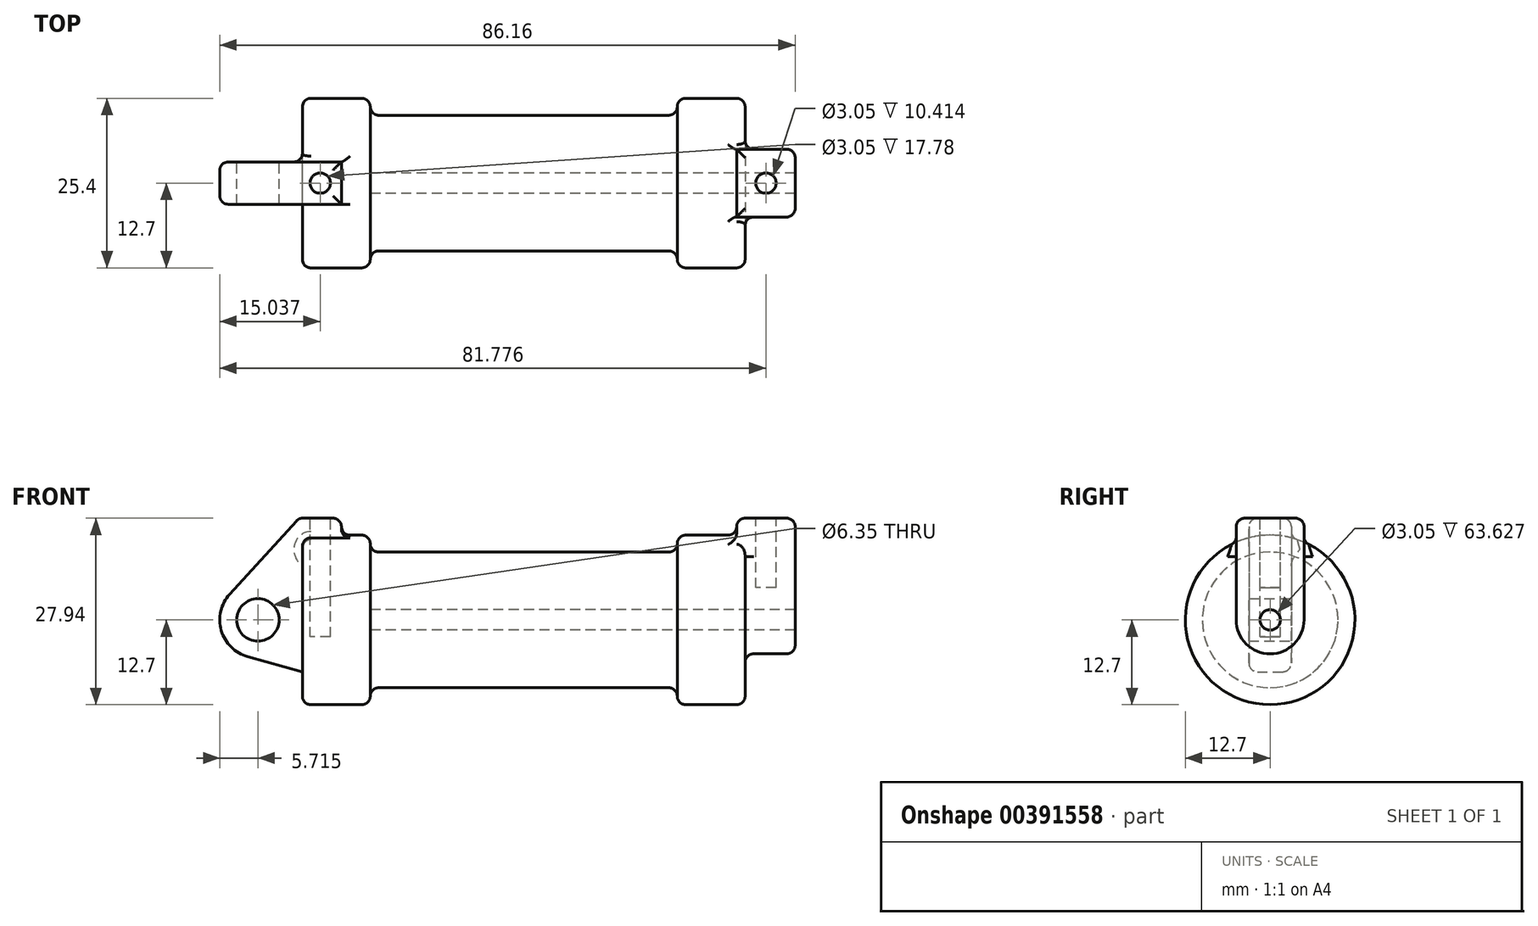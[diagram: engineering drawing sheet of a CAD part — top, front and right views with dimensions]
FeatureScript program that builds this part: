
annotation { "Feature Type Name" : "Feature", "Feature Type Description" : "" }
export const myFeature = defineFeature(function(context is Context, id is Id, definition is map)
    precondition{}
    {
        {
            var Q0;
            Q0=qCreatedBy(makeId("Front.planeOp"),FACE);
            var sketch = newSketch(context, id + "F0", { "sketchPlane" : qUnion([Q0])});
            skLineSegment(sketch, "E0", {"start": v(0, 0) * mm, "end": v(0, 12.7) * mm});
            skLineSegment(sketch, "E1", {"start": v(0, 12.7) * mm, "end": v(10.16, 12.7) * mm});
            skLineSegment(sketch, "E2", {"start": v(10.16, 12.7) * mm, "end": v(10.16, 10.16) * mm});
            skLineSegment(sketch, "E3", {"start": v(10.16, 10.16) * mm, "end": v(56.13, 10.16) * mm});
            skLineSegment(sketch, "E4", {"start": v(56.13, 10.16) * mm, "end": v(56.13, 12.7) * mm});
            skLineSegment(sketch, "E5", {"start": v(56.13, 12.7) * mm, "end": v(66.3, 12.7) * mm});
            skLineSegment(sketch, "E6", {"start": v(66.3, 12.7) * mm, "end": v(66.3, 0) * mm});
            skLineSegment(sketch, "E7", {"start": v(66.3, 0) * mm, "end": v(0, 0) * mm});
            skLineSegment(sketch, "E8", {"start": v(5.84, 15.24) * mm, "end": v(-0.5, 15.24) * mm});
            skLineSegment(sketch, "E9", {"start": v(-0.5, 15.24) * mm, "end": v(-10.88, 3.85) * mm});
            skLineSegment(sketch, "E10", {"start": v(0, 0) * mm, "end": v(-6.65, 0) * mm});
            skCircle(sketch, "E11", {"center": v(-6.65, 0) * mm, "radius": 5.72 * mm});
            skCircle(sketch, "E12", {"center": v(-6.65, 0) * mm, "radius": 3.18 * mm});
            skLineSegment(sketch, "E13", {"start": v(5.84, 15.24) * mm, "end": v(5.84, -9.4) * mm});
            skLineSegment(sketch, "E14", {"start": v(5.84, -9.4) * mm, "end": v(-8.18, -5.5) * mm});
            skSolve(sketch);
        }
        {
            var Q0;
            {var subQ0=sQuery(id+"F0.wireOp",EDGE,"E2");Q0=makeQuery(id+"F0.imprint","IMPRINT",FACE,{"disambiguationData":[TD([[makeQuery(id+"F0.imprint","IMPRINT",EDGE,{"derivedFrom":subQ0}),-1.0]])]});}
            var Q1;
            {var subQ0=sQuery(id+"F0.wireOp",EDGE,"E2");Q1=makeQuery(id+"F0.imprint","IMPRINT",FACE,{"disambiguationData":[TD([[makeQuery(id+"F0.imprint","IMPRINT",EDGE,{"derivedFrom":subQ0}),-1.0]])]});}
            var Q2;
            {var subQ0=sQuery(id+"F0.wireOp",EDGE,"E0");Q2=makeQuery(id+"F0.imprint","IMPRINT",FACE,{"disambiguationData":[TD([[makeQuery(id+"F0.imprint","IMPRINT",EDGE,{"derivedFrom":subQ0}),-1.0]])]});}
            var Q3;
            Q3=sQuery(id+"F0.wireOp",EDGE,"E7");
            revolve(context, id + "F1", {"entities" : qUnion([Q0, Q1, Q2]), "axis" : qUnion([Q3]), "revolveType" : RevolveType.FULL});
        }
        {
            var Q0;
            {var subQ1=sQuery(id+"F0.wireOp",EDGE,"E0");Q0=makeQuery(id+"F0.imprint","IMPRINT",FACE,{"disambiguationData":[TD([[makeQuery(id+"F0.imprint","IMPRINT",EDGE,{"derivedFrom":subQ1}),1.0]])]});}
            var Q1;
            {var subQ0=sQuery(id+"F0.wireOp",EDGE,"E14");Q1=makeQuery(id+"F0.imprint","IMPRINT",FACE,{"disambiguationData":[TD([[makeQuery(id+"F0.imprint","IMPRINT",EDGE,{"derivedFrom":subQ0}),-1.0]])]});}
            var Q2;
            {var subQ5=sQuery(id+"F0.wireOp",EDGE,"E12");Q2=makeQuery(id+"F0.imprint","IMPRINT",FACE,{"disambiguationData":[TD([[makeQuery(id+"F0.imprint","IMPRINT",EDGE,{"derivedFrom":subQ5}),-1.0]])]});}
            var Q3;
            {var subQ0=sQuery(id+"F0.wireOp",EDGE,"E0");Q3=makeQuery(id+"F0.imprint","IMPRINT",FACE,{"disambiguationData":[TD([[makeQuery(id+"F0.imprint","IMPRINT",EDGE,{"derivedFrom":subQ0}),-1.0]])]});}
            extrude(context, id + "F2", {"entities" : qUnion([Q0, Q1, Q2, Q3]), "operationType" : NewBodyOperationType.ADD, "endBound" : BoundingType.SYMMETRIC, "depth" : 6.35 * mm});
        }
        {
            var Q0;
            Q0=makeQuery(id+"F1.opRevolve","SWEPT_FACE",FACE,{"disambiguationData":[OSD([sQuery(id+"F0.wireOp",EDGE,"E6")])]});
            var sketch = newSketch(context, id + "F3", { "sketchPlane" : qUnion([Q0])});
            skArc(sketch, "E15", {"start": v(-5.08, 0) * mm, "mid": v(0, -5.08) * mm, "end": v(5.08, 0) * mm});
            skCircle(sketch, "E16", {"center": v(0, 0) * mm, "radius": 1.52 * mm});
            skLineSegment(sketch, "E17", {"start": v(5.08, 0) * mm, "end": v(5.08, 15.24) * mm});
            skLineSegment(sketch, "E18", {"start": v(-5.08, 0) * mm, "end": v(-5.08, 15.24) * mm});
            skLineSegment(sketch, "E19", {"start": v(-5.08, 15.24) * mm, "end": v(5.08, 15.24) * mm});
            skSolve(sketch);
        }
        {
            var Q0;
            Q0 = qSketchRegion(id + "F3", true);
            extrude(context, id + "F4", {"entities" : qUnion([Q0]), "operationType" : NewBodyOperationType.ADD, "depth" : 7.5 * mm, "hasSecondDirection" : true, "secondDirectionOppositeDirection" : true, "secondDirectionDepth" : 1.27 * mm});
        }
        {
            var Q0;
            Q0=makeQuery(id+"F3.imprint","IMPRINT",FACE,{"disambiguationData":[TD([[makeQuery(id+"F3.imprint","IMPRINT",EDGE,{"derivedFrom":sQuery(id+"F3.wireOp",EDGE,"E16")}),1.0]])]});
            var Q1;
            Q1=makeQuery(id+"F1.opRevolve","SWEPT_FACE",FACE,{"disambiguationData":[OSD([sQuery(id+"F0.wireOp",EDGE,"E2")])]});
            extrude(context, id + "F5", {"entities" : qUnion([Q0]), "operationType" : NewBodyOperationType.REMOVE, "endBound" : BoundingType.UP_TO_SURFACE, "oppositeDirection" : true, "endBoundEntityFace" : qUnion([Q1]), "depth" : 25.4 * mm});
        }
        {
            var Q0;
            Q0=makeQuery(id+"F4.opExtrude","SWEPT_FACE",FACE,{"disambiguationData":[OSD([sQuery(id+"F3.wireOp",EDGE,"E19")])]});
            var sketch = newSketch(context, id + "F6", { "sketchPlane" : qUnion([Q0])});
            skLineSegment(sketch, "E20.bottom", {"start": v(65.02, 5.08) * mm, "end": v(73.79, 5.08) * mm});
            skLineSegment(sketch, "E20.top", {"start": v(65.02, -5.08) * mm, "end": v(73.79, -5.08) * mm});
            skLineSegment(sketch, "E20.left", {"start": v(65.02, 5.08) * mm, "end": v(65.02, -5.08) * mm});
            skLineSegment(sketch, "E20.right", {"start": v(73.79, 5.08) * mm, "end": v(73.79, -5.08) * mm});
            skCircle(sketch, "E21", {"center": v(69.4, 0) * mm, "radius": 1.52 * mm});
            skPoint(sketch, "E21.centerSnap0", {"position": v(73.79, 0) * mm});
            skPoint(sketch, "E21.centerSnap1", {"position": v(69.4, 5.08) * mm});
            skSolve(sketch);
        }
        {
            var Q0;
            Q0=makeQuery(id+"F6.imprint","IMPRINT",FACE,{"disambiguationData":[TD([[makeQuery(id+"F6.imprint","IMPRINT",EDGE,{"derivedFrom":sQuery(id+"F6.wireOp",EDGE,"E21")}),1.0]])]});
            extrude(context, id + "F7", {"entities" : qUnion([Q0]), "operationType" : NewBodyOperationType.REMOVE, "oppositeDirection" : true, "depth" : 10.4 * mm});
        }
        {
            var Q0;
            Q0=makeQuery(id+"F2.opExtrude","SWEPT_FACE",FACE,{"disambiguationData":[OSD([sQuery(id+"F0.wireOp",EDGE,"E8")])]});
            var sketch = newSketch(context, id + "F8", { "sketchPlane" : qUnion([Q0])});
            skLineSegment(sketch, "E22.bottom", {"start": v(-0.5, 3.18) * mm, "end": v(5.84, 3.18) * mm});
            skLineSegment(sketch, "E22.top", {"start": v(-0.5, -3.18) * mm, "end": v(5.84, -3.18) * mm});
            skLineSegment(sketch, "E22.left", {"start": v(-0.5, 3.18) * mm, "end": v(-0.5, -3.18) * mm});
            skLineSegment(sketch, "E22.right", {"start": v(5.84, 3.18) * mm, "end": v(5.84, -3.18) * mm});
            skCircle(sketch, "E23", {"center": v(2.67, 0) * mm, "radius": 1.52 * mm});
            skPoint(sketch, "E23.centerSnap0", {"position": v(2.67, 3.18) * mm});
            skPoint(sketch, "E23.centerSnap1", {"position": v(5.84, 0) * mm});
            skSolve(sketch);
        }
        {
            var Q0;
            Q0=makeQuery(id+"F8.imprint","IMPRINT",FACE,{"disambiguationData":[TD([[makeQuery(id+"F8.imprint","IMPRINT",EDGE,{"derivedFrom":sQuery(id+"F8.wireOp",EDGE,"E23")}),1.0]])]});
            extrude(context, id + "F9", {"entities" : qUnion([Q0]), "operationType" : NewBodyOperationType.REMOVE, "oppositeDirection" : true, "depth" : 17.78 * mm});
        }
        {
            var Q0;
            Q0=makeQuery(id+"F1.opRevolve","SWEPT_EDGE",EDGE,{"disambiguationData":[OSD([sQuery(id+"F0.wireOp",EDGE,"E1"),sQuery(id+"F0.wireOp",EDGE,"E2")])]});
            var Q1;
            Q1=makeQuery(id+"F1.opRevolve","SWEPT_EDGE",EDGE,{"disambiguationData":[OSD([sQuery(id+"F0.wireOp",EDGE,"E4"),sQuery(id+"F0.wireOp",EDGE,"E5")])]});
            var Q2;
            Q2=makeQuery(id+"F1.opRevolve","SWEPT_EDGE",EDGE,{"disambiguationData":[OSD([sQuery(id+"F0.wireOp",EDGE,"E5"),sQuery(id+"F0.wireOp",EDGE,"E6")])]});
            var Q3;
            Q3=makeQuery(id+"F1.opRevolve","SWEPT_EDGE",EDGE,{"disambiguationData":[OSD([sQuery(id+"F0.wireOp",EDGE,"E0"),sQuery(id+"F0.wireOp",EDGE,"E1")])]});
            var Q4;
            Q4=makeQuery(id+"F2.opExtrude","CAP_EDGE",EDGE,{"disambiguationData":[OSD([sQuery(id+"F0.wireOp",EDGE,"E14")])],"isStart":true});
            var Q5;
            Q5=makeQuery(id+"F2.opExtrude","CAP_EDGE",EDGE,{"disambiguationData":[OSD([sQuery(id+"F0.wireOp",EDGE,"E11")])],"isStart":true});
            var Q6;
            Q6=makeQuery(id+"F2.opExtrude","CAP_EDGE",EDGE,{"disambiguationData":[OSD([sQuery(id+"F0.wireOp",EDGE,"E14")])],"isStart":false});
            var Q7;
            Q7=makeQuery(id+"F2.opExtrude","CAP_EDGE",EDGE,{"disambiguationData":[OSD([sQuery(id+"F0.wireOp",EDGE,"E11")])],"isStart":false});
            var Q8;
            Q8=makeQuery(id+"F2.opExtrude","CAP_EDGE",EDGE,{"disambiguationData":[OSD([sQuery(id+"F0.wireOp",EDGE,"E8")])],"isStart":false});
            var Q9;
            Q9=makeQuery(id+"F2.opExtrude","SWEPT_EDGE",EDGE,{"disambiguationData":[OSD([sQuery(id+"F0.wireOp",EDGE,"E8"),sQuery(id+"F0.wireOp",EDGE,"E13")])]});
            var Q10;
            Q10=makeQuery(id+"F2.opExtrude","CAP_EDGE",EDGE,{"disambiguationData":[OSD([sQuery(id+"F0.wireOp",EDGE,"E8")])],"isStart":true});
            var Q11;
            Q11=makeQuery(id+"F2.opExtrude","SWEPT_EDGE",EDGE,{"disambiguationData":[OSD([sQuery(id+"F0.wireOp",EDGE,"E8"),sQuery(id+"F0.wireOp",EDGE,"E9")])]});
            var Q12;
            Q12=makeQuery(id+"F4.opExtrude","CAP_EDGE",EDGE,{"disambiguationData":[OSD([sQuery(id+"F3.wireOp",EDGE,"E19")])],"isStart":true});
            var Q13;
            Q13=makeQuery(id+"F4.opExtrude","SWEPT_EDGE",EDGE,{"disambiguationData":[OSD([sQuery(id+"F3.wireOp",EDGE,"E18"),sQuery(id+"F3.wireOp",EDGE,"E19")])]});
            var Q14;
            Q14=makeQuery(id+"F4.opExtrude","CAP_EDGE",EDGE,{"disambiguationData":[OSD([sQuery(id+"F3.wireOp",EDGE,"E19")])],"isStart":false});
            var Q15;
            Q15=makeQuery(id+"F4.opExtrude","SWEPT_EDGE",EDGE,{"disambiguationData":[OSD([sQuery(id+"F3.wireOp",EDGE,"E17"),sQuery(id+"F3.wireOp",EDGE,"E19")])]});
            var Q16;
            Q16=makeQuery(id+"F4.opExtrude","CAP_EDGE",EDGE,{"disambiguationData":[OSD([sQuery(id+"F3.wireOp",EDGE,"E18")])],"isStart":false});
            var Q17;
            Q17=makeQuery(id+"F4.boolean.opBoolean","INTERSECT",EDGE,{"derivedFrom":[makeQuery(id+"F1.opRevolve","SWEPT_FACE",FACE,{"disambiguationData":[OSD([sQuery(id+"F0.wireOp",EDGE,"E5")])]}),makeQuery(id+"F4.opExtrude","CAP_FACE",FACE,{"disambiguationData":[OSD([sQuery(id+"F3.wireOp",EDGE,"E15"),sQuery(id+"F3.wireOp",EDGE,"E16"),sQuery(id+"F3.wireOp",EDGE,"E17"),sQuery(id+"F3.wireOp",EDGE,"E18"),sQuery(id+"F3.wireOp",EDGE,"E19")])],"isStart":true})]});
            var Q18;
            Q18=makeQuery(id+"F1.opRevolve","SWEPT_EDGE",EDGE,{"disambiguationData":[OSD([sQuery(id+"F0.wireOp",EDGE,"E3"),sQuery(id+"F0.wireOp",EDGE,"E4")])]});
            var Q19;
            Q19=makeQuery(id+"F2.boolean.opBoolean","INTERSECT",EDGE,{"derivedFrom":[makeQuery(id+"F1.opRevolve","SWEPT_FACE",FACE,{"disambiguationData":[OSD([sQuery(id+"F0.wireOp",EDGE,"E1")])]}),makeQuery(id+"F2.opExtrude","SWEPT_FACE",FACE,{"disambiguationData":[OSD([sQuery(id+"F0.wireOp",EDGE,"E13")])]})]});
            var Q20;
            Q20=makeQuery(id+"F1.opRevolve","SWEPT_EDGE",EDGE,{"disambiguationData":[OSD([sQuery(id+"F0.wireOp",EDGE,"E2"),sQuery(id+"F0.wireOp",EDGE,"E3")])]});
            var Q21;
            Q21=makeQuery(id+"F2.boolean.opBoolean","INTERSECT",EDGE,{"derivedFrom":[makeQuery(id+"F1.opRevolve","SWEPT_FACE",FACE,{"disambiguationData":[OSD([sQuery(id+"F0.wireOp",EDGE,"E1")])]}),makeQuery(id+"F2.opExtrude","CAP_FACE",FACE,{"disambiguationData":[OSD([sQuery(id+"F0.wireOp",EDGE,"E8"),sQuery(id+"F0.wireOp",EDGE,"E9"),sQuery(id+"F0.wireOp",EDGE,"E11"),sQuery(id+"F0.wireOp",EDGE,"E12"),sQuery(id+"F0.wireOp",EDGE,"E13"),sQuery(id+"F0.wireOp",EDGE,"E14")])],"isStart":true})]});
            fillet(context, id + "F10", {"entities" : qUnion([Q0, Q1, Q2, Q3, Q4, Q5, Q6, Q7, Q8, Q9, Q10, Q11, Q12, Q13, Q14, Q15, Q16, Q17, Q18, Q19, Q20, Q21]), "radius" : 1.27 * mm, "tangentPropagation" : true, "allowEdgeOverflow" : false});
        }
        {
            var Q0;
            Q0=makeQuery(id+"F4.boolean.opBoolean","INTERSECT",EDGE,{"derivedFrom":[makeQuery(id+"F1.opRevolve","SWEPT_FACE",FACE,{"disambiguationData":[OSD([sQuery(id+"F0.wireOp",EDGE,"E6")])]}),makeQuery(id+"F4.opExtrude","SWEPT_FACE",FACE,{"disambiguationData":[OSD([sQuery(id+"F3.wireOp",EDGE,"E18")])]})]});
            fillet(context, id + "F11", {"entities" : qUnion([Q0]), "radius" : 1.27 * mm, "tangentPropagation" : true, "allowEdgeOverflow" : false});
        }
    });
